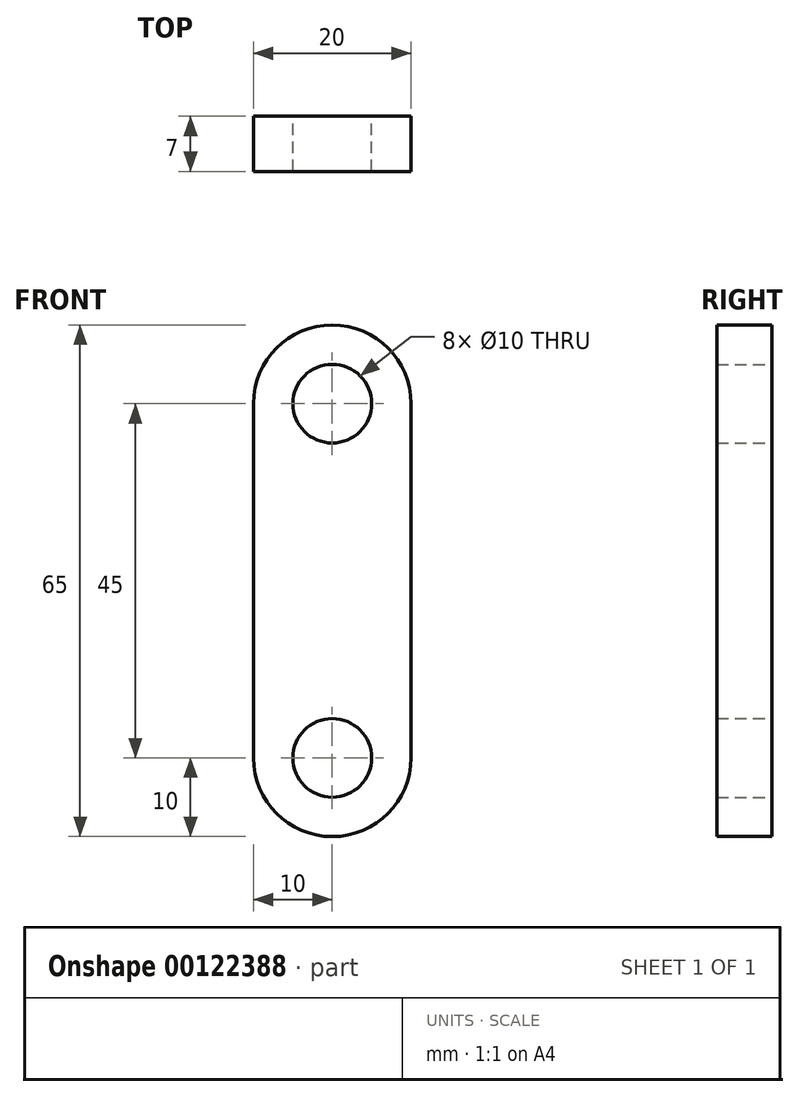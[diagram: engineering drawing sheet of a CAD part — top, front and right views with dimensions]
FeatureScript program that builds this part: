
annotation { "Feature Type Name" : "Feature", "Feature Type Description" : "" }
export const myFeature = defineFeature(function(context is Context, id is Id, definition is map)
    precondition{}
    {
        {
            var Q0;
            Q0=qCreatedBy(makeId("Front.planeOp"),FACE);
            var sketch = newSketch(context, id + "F0", { "sketchPlane" : qUnion([Q0])});
            skLineSegment(sketch, "E0.left", {"start": v(-10, -22.5) * mm, "end": v(-10, 22.5) * mm});
            skLineSegment(sketch, "E0.right", {"start": v(10, -22.5) * mm, "end": v(10, 22.5) * mm});
            skArc(sketch, "E1", {"start": v(-10, -22.5) * mm, "mid": v(0, -32.5) * mm, "end": v(10, -22.5) * mm});
            skArc(sketch, "E2", {"start": v(-10, 22.5) * mm, "mid": v(0, 32.5) * mm, "end": v(10, 22.5) * mm});
            skCircle(sketch, "E3", {"center": v(0, 22.5) * mm, "radius": 5 * mm});
            skCircle(sketch, "E4", {"center": v(0, -22.5) * mm, "radius": 5 * mm});
            skSolve(sketch);
        }
        {
            var Q0;
            Q0 = qSketchRegion(id + "F0", true);
            extrude(context, id + "F1", {"entities" : qUnion([Q0]), "endBound" : BoundingType.SYMMETRIC, "depth" : 7 * mm});
        }
    });
